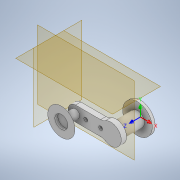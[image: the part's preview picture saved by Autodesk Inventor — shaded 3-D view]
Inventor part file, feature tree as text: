
AUTODESK INVENTOR PART (.ipt)
format: ipt  version: 2022 (Build 260153000, 153)  size: 183,808 bytes
history: native  units: mm
features: other x9, sketch x5, extrude x4, plane x1, revolve x1
ambient origin geometry x8: Origin, YZ Plane, XZ Plane, XY Plane, X Axis, Y Axis, Z Axis, Center Point
bodies: Body1 (feature_tree)
feature tree (20):
  other  "Sólido1"
  extrude  "Extrusión1"  Depth=24.0mm
  extrude  "Extrusión2"  Depth=50.0mm
  extrude  "Extrusión3"  Depth=9.0mm TaperAngle=0.0deg
  plane  "Plano de trabajo1"
  revolve  "Revolución1"  [1 undecoded]
  extrude  "Extrusión5"  Depth=11.0mm
  other  "SCU1"
  sketch  "Boceto1"  dims[d11=9.0mm d12=0.0mm d13=24.0mm]
  sketch  "Boceto2"  dims[d14=36.0mm d15=0.0mm d16=50.0mm]
  sketch  "Boceto3"  dims[d17=5.0mm d18=0.0mm d19=9.0mm d20=0.0mm]
  sketch  "Boceto7"  dims[d23=14.0mm d24=13.0mm]
  sketch  "Boceto8"  dims[d28=90.0deg d29=22.0mm d30=5.0mm d31=0.0mm d32=0.0mm d33=0.0mm d34=0.0mm d35=0.0mm d36=0.0mm d37=0.0mm d38=46.0mm d39=11.0mm]
  other  "SCU1: Plano YZ"
  other  "SCU1: Plano XZ"
  other  "SCU1: Plano XY"
  other  "SCU1: Eje X"
  other  "SCU1: Eje Y"
  other  "SCU1: Eje Z"
  other  "SCU1: Centro"
note: 1 required parameter value undecoded (feature->parameter linkage not recoverable at this tier; creation-order binding heuristic only, values carry confidence <= 0.55)
